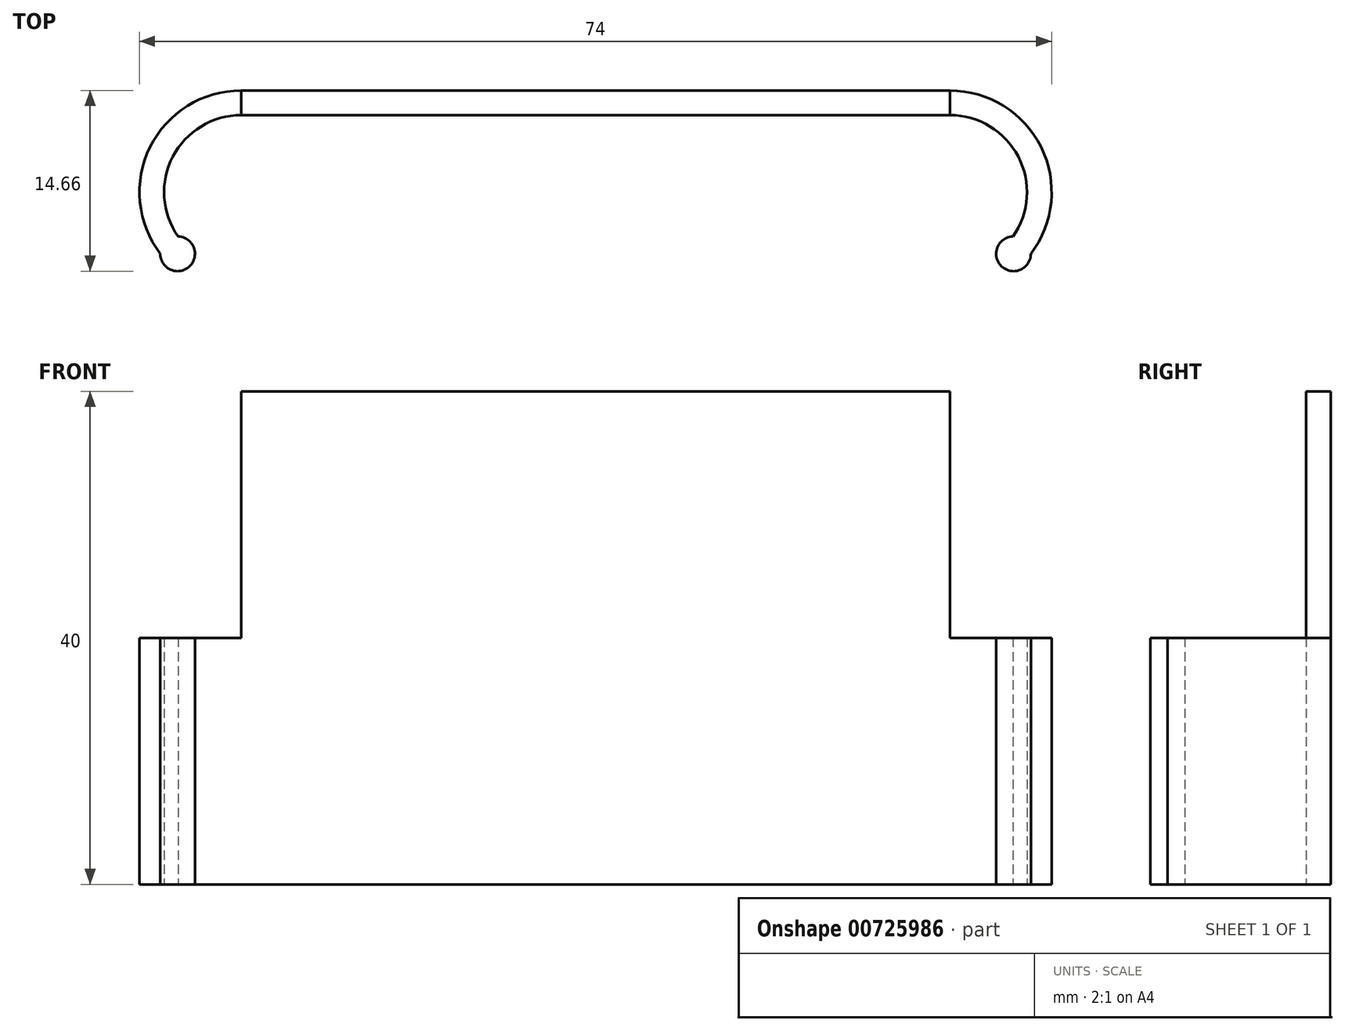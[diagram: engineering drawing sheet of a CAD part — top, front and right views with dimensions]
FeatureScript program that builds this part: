
annotation { "Feature Type Name" : "Feature", "Feature Type Description" : "" }
export const myFeature = defineFeature(function(context is Context, id is Id, definition is map)
    precondition{}
    {
        {
            var Q0;
            Q0=qCreatedBy(makeId("Top.planeOp"),FACE);
            var sketch = newSketch(context, id + "F0", { "sketchPlane" : qUnion([Q0])});
            skLineSegment(sketch, "E0.bottom", {"start": v(-28.75, 6.25) * mm, "end": v(28.75, 6.25) * mm});
            skLineSegment(sketch, "E0.top", {"start": v(-28.75, -6.25) * mm, "end": v(28.75, -6.25) * mm});
            skLineSegment(sketch, "E0.left", {"start": v(-28.75, 6.25) * mm, "end": v(-28.75, -6.25) * mm});
            skLineSegment(sketch, "E0.right", {"start": v(28.75, 6.25) * mm, "end": v(28.75, -6.25) * mm});
            skLineSegment(sketch, "E1.bottom", {"start": v(-28.75, 8.25) * mm, "end": v(28.75, 8.25) * mm});
            skLineSegment(sketch, "E1.top", {"start": v(-28.75, -8.25) * mm, "end": v(28.75, -8.25) * mm});
            skLineSegment(sketch, "E1.left", {"start": v(-28.75, 8.25) * mm, "end": v(-28.75, -8.25) * mm});
            skLineSegment(sketch, "E1.right", {"start": v(28.75, 8.25) * mm, "end": v(28.75, -8.25) * mm});
            skCircle(sketch, "E2", {"center": v(28.75, 0) * mm, "radius": 6.25 * mm});
            skCircle(sketch, "E3", {"center": v(28.75, 0) * mm, "radius": 8.25 * mm});
            skCircle(sketch, "E4", {"center": v(-28.75, 0) * mm, "radius": 6.25 * mm});
            skCircle(sketch, "E5", {"center": v(-28.75, 0) * mm, "radius": 8.25 * mm});
            skLineSegment(sketch, "E6", {"start": v(-47.39, -5) * mm, "end": v(64.54, -5) * mm});
            skPoint(sketch, "E7", {"position": v(-33.9, -5) * mm});
            skPoint(sketch, "E8", {"position": v(-35.31, -5) * mm});
            skPoint(sketch, "E9", {"position": v(-32.5, -5) * mm});
            skPoint(sketch, "E10", {"position": v(32.5, -5) * mm});
            skPoint(sketch, "E11", {"position": v(35.31, -5) * mm});
            skPoint(sketch, "E12", {"position": v(33.9, -5) * mm});
            skCircle(sketch, "E13", {"center": v(33.9, -5) * mm, "radius": 1.4 * mm});
            skCircle(sketch, "E14", {"center": v(-33.9, -5) * mm, "radius": 1.4 * mm});
            skPoint(sketch, "E15", {"position": v(-35, 0) * mm});
            skPoint(sketch, "E16", {"position": v(35, 0) * mm});
            skSolve(sketch);
        }
        {
            var Q0;
            {var subQ5=sQuery(id+"F0.wireOp",EDGE,"E1.bottom");Q0=makeQuery(id+"F0.imprint","IMPRINT",FACE,{"disambiguationData":[TD([[makeQuery(id+"F0.imprint","IMPRINT",EDGE,{"derivedFrom":subQ5}),-1.0]])]});}
            var Q1;
            {var subQ1=sQuery(id+"F0.wireOp",EDGE,"E0.bottom");var subQ3=sQuery(id+"F0.wireOp",EDGE,"E5");var subQ4=makeQuery(id+"F0.imprint","INTERSECT",VERTEX,{"derivedFrom":[subQ1,subQ3]});Q1=makeQuery(id+"F0.imprint","IMPRINT",FACE,{"disambiguationData":[TD([[makeQuery(id+"F0.imprint","IMPRINT",EDGE,{"disambiguationData":[TD([[subQ4,1.0]])],"derivedFrom":subQ1}),1.0]])]});}
            var Q2;
            {var subQ1=sQuery(id+"F0.wireOp",EDGE,"E0.bottom");var subQ3=sQuery(id+"F0.wireOp",EDGE,"E3");var subQ4=makeQuery(id+"F0.imprint","INTERSECT",VERTEX,{"derivedFrom":[subQ1,subQ3]});Q2=makeQuery(id+"F0.imprint","IMPRINT",FACE,{"disambiguationData":[TD([[makeQuery(id+"F0.imprint","IMPRINT",EDGE,{"disambiguationData":[TD([[subQ4,-1.0]])],"derivedFrom":subQ1}),1.0]])]});}
            var Q3;
            {var subQ0=sQuery(id+"F0.wireOp",EDGE,"E4");var subQ5=sQuery(id+"F0.wireOp",EDGE,"E14");var subQ6=makeQuery(id+"F0.imprint","INTERSECT",VERTEX,{"derivedFrom":[subQ0,subQ5]});Q3=makeQuery(id+"F0.imprint","IMPRINT",FACE,{"disambiguationData":[TD([[makeQuery(id+"F0.imprint","IMPRINT",EDGE,{"disambiguationData":[TD([[subQ6,1.0]])],"derivedFrom":subQ0}),-1.0]])]});}
            var Q4;
            {var subQ0=sQuery(id+"F0.wireOp",EDGE,"E14");var subQ1=sQuery(id+"F0.wireOp",EDGE,"E4");var subQ2=makeQuery(id+"F0.imprint","INTERSECT",VERTEX,{"derivedFrom":[subQ1,subQ0]});Q4=makeQuery(id+"F0.imprint","IMPRINT",FACE,{"disambiguationData":[TD([[makeQuery(id+"F0.imprint","IMPRINT",EDGE,{"disambiguationData":[TD([[subQ2,-1.0]])],"derivedFrom":subQ1}),-1.0]])]});}
            var Q5;
            {var subQ0=sQuery(id+"F0.wireOp",EDGE,"E14");var subQ1=sQuery(id+"F0.wireOp",EDGE,"E5");var subQ2=makeQuery(id+"F0.imprint","INTERSECT",VERTEX,{"derivedFrom":[subQ1,subQ0]});Q5=makeQuery(id+"F0.imprint","IMPRINT",FACE,{"disambiguationData":[TD([[makeQuery(id+"F0.imprint","IMPRINT",EDGE,{"disambiguationData":[TD([[subQ2,1.0]])],"derivedFrom":subQ1}),-1.0]])]});}
            var Q6;
            {var subQ0=sQuery(id+"F0.wireOp",EDGE,"E14");var subQ1=sQuery(id+"F0.wireOp",EDGE,"E5");var subQ2=makeQuery(id+"F0.imprint","INTERSECT",VERTEX,{"derivedFrom":[subQ1,subQ0]});Q6=makeQuery(id+"F0.imprint","IMPRINT",FACE,{"disambiguationData":[TD([[makeQuery(id+"F0.imprint","IMPRINT",EDGE,{"disambiguationData":[TD([[subQ2,1.0]])],"derivedFrom":subQ1}),1.0]])]});}
            var Q7;
            {var subQ0=sQuery(id+"F0.wireOp",EDGE,"E14");var subQ1=sQuery(id+"F0.wireOp",EDGE,"E4");var subQ2=makeQuery(id+"F0.imprint","INTERSECT",VERTEX,{"derivedFrom":[subQ1,subQ0]});Q7=makeQuery(id+"F0.imprint","IMPRINT",FACE,{"disambiguationData":[TD([[makeQuery(id+"F0.imprint","IMPRINT",EDGE,{"disambiguationData":[TD([[subQ2,-1.0]])],"derivedFrom":subQ1}),1.0]])]});}
            var Q8;
            {var subQ0=sQuery(id+"F0.wireOp",EDGE,"E2");var subQ5=sQuery(id+"F0.wireOp",EDGE,"E13");var subQ7=makeQuery(id+"F0.imprint","INTERSECT",VERTEX,{"derivedFrom":[subQ0,subQ5]});Q8=makeQuery(id+"F0.imprint","IMPRINT",FACE,{"disambiguationData":[TD([[makeQuery(id+"F0.imprint","IMPRINT",EDGE,{"disambiguationData":[TD([[subQ7,-1.0]])],"derivedFrom":subQ0}),-1.0]])]});}
            var Q9;
            {var subQ0=sQuery(id+"F0.wireOp",EDGE,"E13");var subQ1=sQuery(id+"F0.wireOp",EDGE,"E3");var subQ2=makeQuery(id+"F0.imprint","INTERSECT",VERTEX,{"derivedFrom":[subQ1,subQ0]});Q9=makeQuery(id+"F0.imprint","IMPRINT",FACE,{"disambiguationData":[TD([[makeQuery(id+"F0.imprint","IMPRINT",EDGE,{"disambiguationData":[TD([[subQ2,-1.0]])],"derivedFrom":subQ1}),1.0]])]});}
            var Q10;
            {var subQ0=sQuery(id+"F0.wireOp",EDGE,"E13");var subQ1=sQuery(id+"F0.wireOp",EDGE,"E2");var subQ2=makeQuery(id+"F0.imprint","INTERSECT",VERTEX,{"derivedFrom":[subQ1,subQ0]});Q10=makeQuery(id+"F0.imprint","IMPRINT",FACE,{"disambiguationData":[TD([[makeQuery(id+"F0.imprint","IMPRINT",EDGE,{"disambiguationData":[TD([[subQ2,1.0]])],"derivedFrom":subQ1}),-1.0]])]});}
            var Q11;
            {var subQ0=sQuery(id+"F0.wireOp",EDGE,"E13");var subQ1=sQuery(id+"F0.wireOp",EDGE,"E2");var subQ2=makeQuery(id+"F0.imprint","INTERSECT",VERTEX,{"derivedFrom":[subQ1,subQ0]});Q11=makeQuery(id+"F0.imprint","IMPRINT",FACE,{"disambiguationData":[TD([[makeQuery(id+"F0.imprint","IMPRINT",EDGE,{"disambiguationData":[TD([[subQ2,1.0]])],"derivedFrom":subQ1}),1.0]])]});}
            var Q12;
            {var subQ0=sQuery(id+"F0.wireOp",EDGE,"E13");var subQ1=sQuery(id+"F0.wireOp",EDGE,"E3");var subQ2=makeQuery(id+"F0.imprint","INTERSECT",VERTEX,{"derivedFrom":[subQ1,subQ0]});Q12=makeQuery(id+"F0.imprint","IMPRINT",FACE,{"disambiguationData":[TD([[makeQuery(id+"F0.imprint","IMPRINT",EDGE,{"disambiguationData":[TD([[subQ2,-1.0]])],"derivedFrom":subQ1}),-1.0]])]});}
            extrude(context, id + "F1", {"entities" : qUnion([Q0, Q1, Q2, Q3, Q4, Q5, Q6, Q7, Q8, Q9, Q10, Q11, Q12]), "endBound" : BoundingType.SYMMETRIC, "depth" : 40 * mm, "offsetDistance" : 25 * mm});
        }
        {
            var Q0;
            Q0=qCreatedBy(makeId("Front.planeOp"),FACE);
            var sketch = newSketch(context, id + "F2", { "sketchPlane" : qUnion([Q0])});
            skLineSegment(sketch, "E17.0", {"start": v(-28.75, 20) * mm, "end": v(28.75, 20) * mm});
            skLineSegment(sketch, "E18.bottom", {"start": v(-46.96, 0) * mm, "end": v(47.16, 0) * mm});
            skLineSegment(sketch, "E18.top", {"start": v(-46.96, 20) * mm, "end": v(47.16, 20) * mm});
            skLineSegment(sketch, "E18.left", {"start": v(-46.96, 0) * mm, "end": v(-46.96, 20) * mm});
            skLineSegment(sketch, "E18.right", {"start": v(47.16, 0) * mm, "end": v(47.16, 20) * mm});
            skLineSegment(sketch, "E19.0", {"start": v(-28.75, 20) * mm, "end": v(-28.75, -20) * mm});
            skLineSegment(sketch, "E20.0", {"start": v(28.75, 20) * mm, "end": v(28.75, -20) * mm});
            skSolve(sketch);
        }
        {
            var Q0;
            Q0=makeQuery(id+"F2.imprint","IMPRINT",FACE,{"disambiguationData":[TD([[makeQuery(id+"F2.imprint","IMPRINT",EDGE,{"derivedFrom":sQuery(id+"F2.wireOp",EDGE,"E18.bottom")}),1.0]])]});
            extrude(context, id + "F3", {"entities" : qUnion([Q0]), "operationType" : NewBodyOperationType.REMOVE, "depth" : 25 * mm, "offsetDistance" : 25 * mm});
        }
        {
            var Q0;
            {var subQ0=sQuery(id+"F2.wireOp",EDGE,"E18.left");Q0=makeQuery(id+"F2.imprint","IMPRINT",FACE,{"disambiguationData":[TD([[makeQuery(id+"F2.imprint","IMPRINT",EDGE,{"derivedFrom":subQ0}),-1.0]])]});}
            var Q1;
            {var subQ0=sQuery(id+"F2.wireOp",EDGE,"E18.right");Q1=makeQuery(id+"F2.imprint","IMPRINT",FACE,{"disambiguationData":[TD([[makeQuery(id+"F2.imprint","IMPRINT",EDGE,{"derivedFrom":subQ0}),1.0]])]});}
            extrude(context, id + "F4", {"entities" : qUnion([Q0, Q1]), "operationType" : NewBodyOperationType.REMOVE, "oppositeDirection" : true, "depth" : 25 * mm, "offsetDistance" : 25 * mm});
        }
    });
